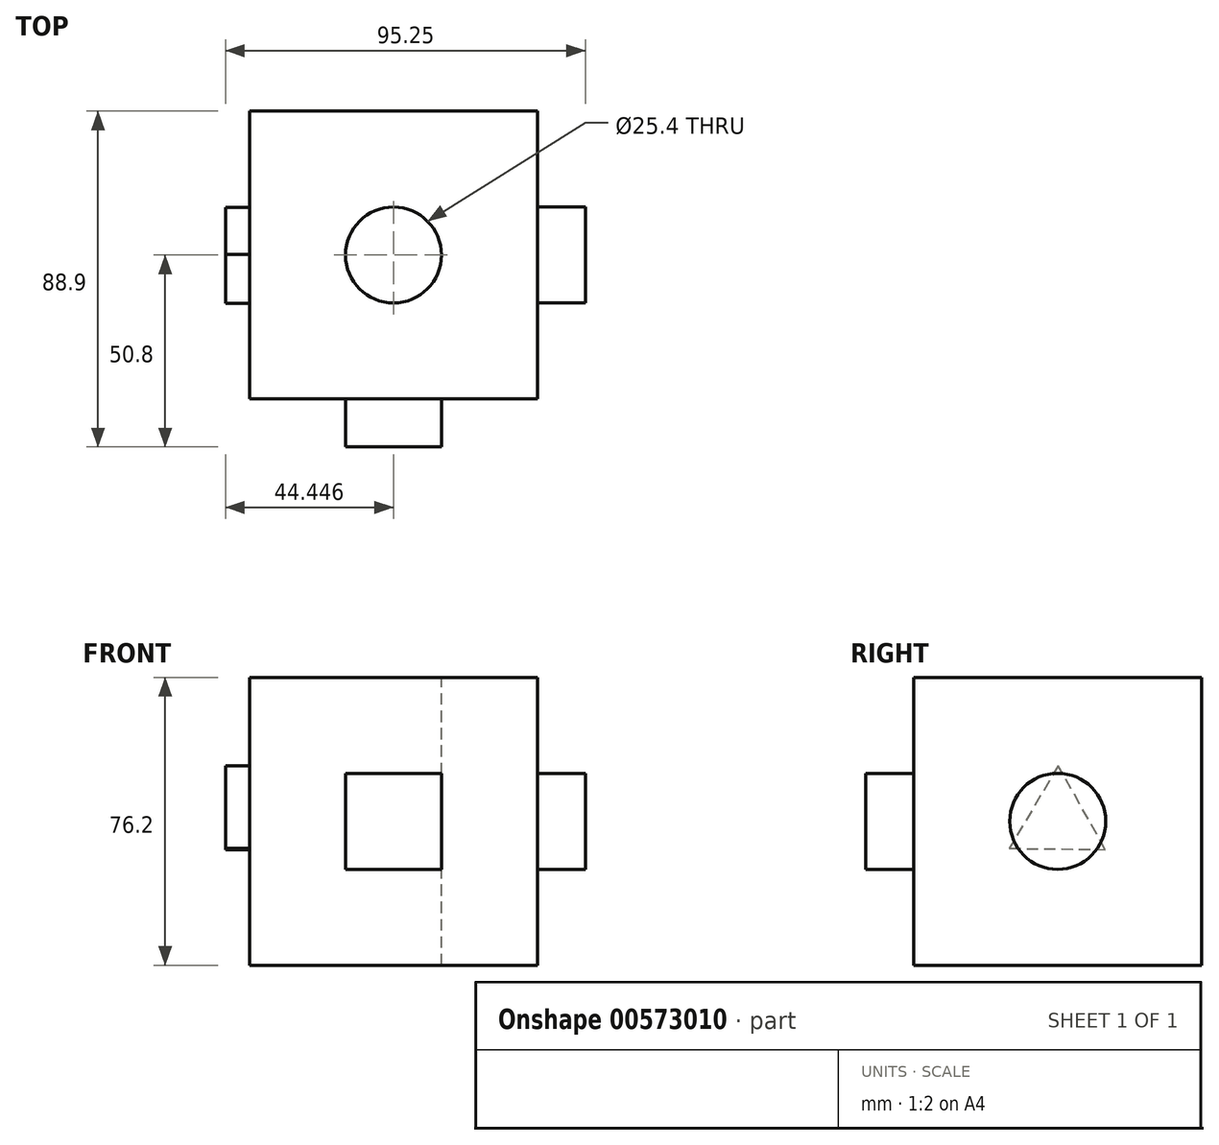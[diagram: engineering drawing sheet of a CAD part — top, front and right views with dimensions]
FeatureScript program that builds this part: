
annotation { "Feature Type Name" : "Feature", "Feature Type Description" : "" }
export const myFeature = defineFeature(function(context is Context, id is Id, definition is map)
    precondition{}
    {
        {
            var Q0;
            Q0=qCreatedBy(makeId("Front.planeOp"),FACE);
            var sketch = newSketch(context, id + "F0", { "sketchPlane" : qUnion([Q0])});
            skLineSegment(sketch, "E0.bottom", {"start": v(-31.46, -38.71) * mm, "end": v(44.74, -38.71) * mm});
            skLineSegment(sketch, "E0.top", {"start": v(-31.46, 37.49) * mm, "end": v(44.74, 37.49) * mm});
            skLineSegment(sketch, "E0.left", {"start": v(-31.46, -38.71) * mm, "end": v(-31.46, 37.49) * mm});
            skLineSegment(sketch, "E0.right", {"start": v(44.74, -38.71) * mm, "end": v(44.74, 37.49) * mm});
            skSolve(sketch);
        }
        {
            var Q0;
            Q0=makeQuery(id+"F0.imprint","IMPRINT",FACE,{"disambiguationData":[TD([[makeQuery(id+"F0.imprint","IMPRINT",EDGE,{"derivedFrom":sQuery(id+"F0.wireOp",EDGE,"E0.bottom")}),1.0]])]});
            extrude(context, id + "F1", {"entities" : qUnion([Q0]), "depth" : 76.2 * mm, "offsetDistance" : 25.4 * mm});
        }
        {
            var Q0;
            Q0=makeQuery(id+"F1.opExtrude","CAP_FACE",FACE,{"disambiguationData":[OSD([sQuery(id+"F0.wireOp",EDGE,"E0.bottom"),sQuery(id+"F0.wireOp",EDGE,"E0.top"),sQuery(id+"F0.wireOp",EDGE,"E0.left"),sQuery(id+"F0.wireOp",EDGE,"E0.right")])],"isStart":false});
            var sketch = newSketch(context, id + "F2", { "sketchPlane" : qUnion([Q0])});
            skLineSegment(sketch, "E1.bottom", {"start": v(-6.06, -13.31) * mm, "end": v(19.34, -13.31) * mm});
            skLineSegment(sketch, "E1.top", {"start": v(-6.06, 12.09) * mm, "end": v(19.34, 12.09) * mm});
            skLineSegment(sketch, "E1.left", {"start": v(-6.06, -13.31) * mm, "end": v(-6.06, 12.09) * mm});
            skLineSegment(sketch, "E1.right", {"start": v(19.34, -13.31) * mm, "end": v(19.34, 12.09) * mm});
            skSolve(sketch);
        }
        {
            var Q0;
            Q0=makeQuery(id+"F2.imprint","IMPRINT",FACE,{"disambiguationData":[TD([[makeQuery(id+"F2.imprint","IMPRINT",EDGE,{"derivedFrom":sQuery(id+"F2.wireOp",EDGE,"E1.bottom")}),1.0]])]});
            extrude(context, id + "F3", {"entities" : qUnion([Q0]), "operationType" : NewBodyOperationType.ADD, "depth" : 12.7 * mm, "offsetDistance" : 25.4 * mm});
        }
        {
            var Q0;
            Q0=makeQuery(id+"F1.opExtrude","SWEPT_FACE",FACE,{"disambiguationData":[OSD([sQuery(id+"F0.wireOp",EDGE,"E0.right")])]});
            var sketch = newSketch(context, id + "F4", { "sketchPlane" : qUnion([Q0])});
            skCircle(sketch, "E2", {"center": v(-38.1, -0.61) * mm, "radius": 12.7 * mm});
            skSolve(sketch);
        }
        {
            var Q0;
            Q0=makeQuery(id+"F4.imprint","IMPRINT",FACE,{"disambiguationData":[TD([[makeQuery(id+"F4.imprint","IMPRINT",EDGE,{"derivedFrom":sQuery(id+"F4.wireOp",EDGE,"E2")}),1.0]])]});
            extrude(context, id + "F5", {"entities" : qUnion([Q0]), "operationType" : NewBodyOperationType.ADD, "depth" : 12.7 * mm, "offsetDistance" : 25.4 * mm});
        }
        {
            var Q0;
            Q0=makeQuery(id+"F1.opExtrude","SWEPT_FACE",FACE,{"disambiguationData":[OSD([sQuery(id+"F0.wireOp",EDGE,"E0.top")])]});
            var sketch = newSketch(context, id + "F6", { "sketchPlane" : qUnion([Q0])});
            skPoint(sketch, "E3", {"position": v(6.64, -38.1) * mm});
            skSolve(sketch);
        }
        {
            var Q0;
            Q0=sQuery(id+"F6.wireOp",VERTEX,"E3");
            var Q1;
            Q1=makeQuery(id+"F1.opExtrude","SWEPT_BODY",BODY,{"disambiguationData":[OSD([sQuery(id+"F0.wireOp",EDGE,"E0.bottom"),sQuery(id+"F0.wireOp",EDGE,"E0.top"),sQuery(id+"F0.wireOp",EDGE,"E0.left"),sQuery(id+"F0.wireOp",EDGE,"E0.right")])]});
            hole(context, id + "F7", {"style" : HoleStyle.SIMPLE, "endStyle" : HoleEndStyle.THROUGH, "holeDiameter" : 25.4 * mm, "isTappedThrough" : true, "tappedDepth" : 12.7 * mm, "tapClearance" : 3, "locations" : qUnion([Q0]), "scope" : qUnion([Q1])});
        }
        {
            var Q0;
            Q0=makeQuery(id+"F1.opExtrude","SWEPT_FACE",FACE,{"disambiguationData":[OSD([sQuery(id+"F0.wireOp",EDGE,"E0.left")])]});
            var sketch = newSketch(context, id + "F8", { "sketchPlane" : qUnion([Q0])});
            skCircle(sketch, "E4.cCircle", {"center": v(38.1, -0.61) * mm, "radius": 7.33 * mm, "construction": true});
            skLineSegment(sketch, "E4.0", {"start": v(50.89, -7.79) * mm, "end": v(25.5, -8.1) * mm});
            skLineSegment(sketch, "E4.1", {"start": v(25.5, -8.1) * mm, "end": v(37.92, 14.05) * mm});
            skLineSegment(sketch, "E4.2", {"start": v(37.92, 14.05) * mm, "end": v(50.89, -7.79) * mm});
            skPoint(sketch, "E4.0.midPoint", {"position": v(38.19, -7.94) * mm});
            skSolve(sketch);
        }
        {
            var Q0;
            Q0=makeQuery(id+"F8.imprint","IMPRINT",FACE,{"disambiguationData":[TD([[makeQuery(id+"F8.imprint","IMPRINT",EDGE,{"derivedFrom":sQuery(id+"F8.wireOp",EDGE,"E4.0")}),-1.0]])]});
            extrude(context, id + "F9", {"entities" : qUnion([Q0]), "operationType" : NewBodyOperationType.ADD, "depth" : 6.35 * mm, "offsetDistance" : 25.4 * mm});
        }
    });
